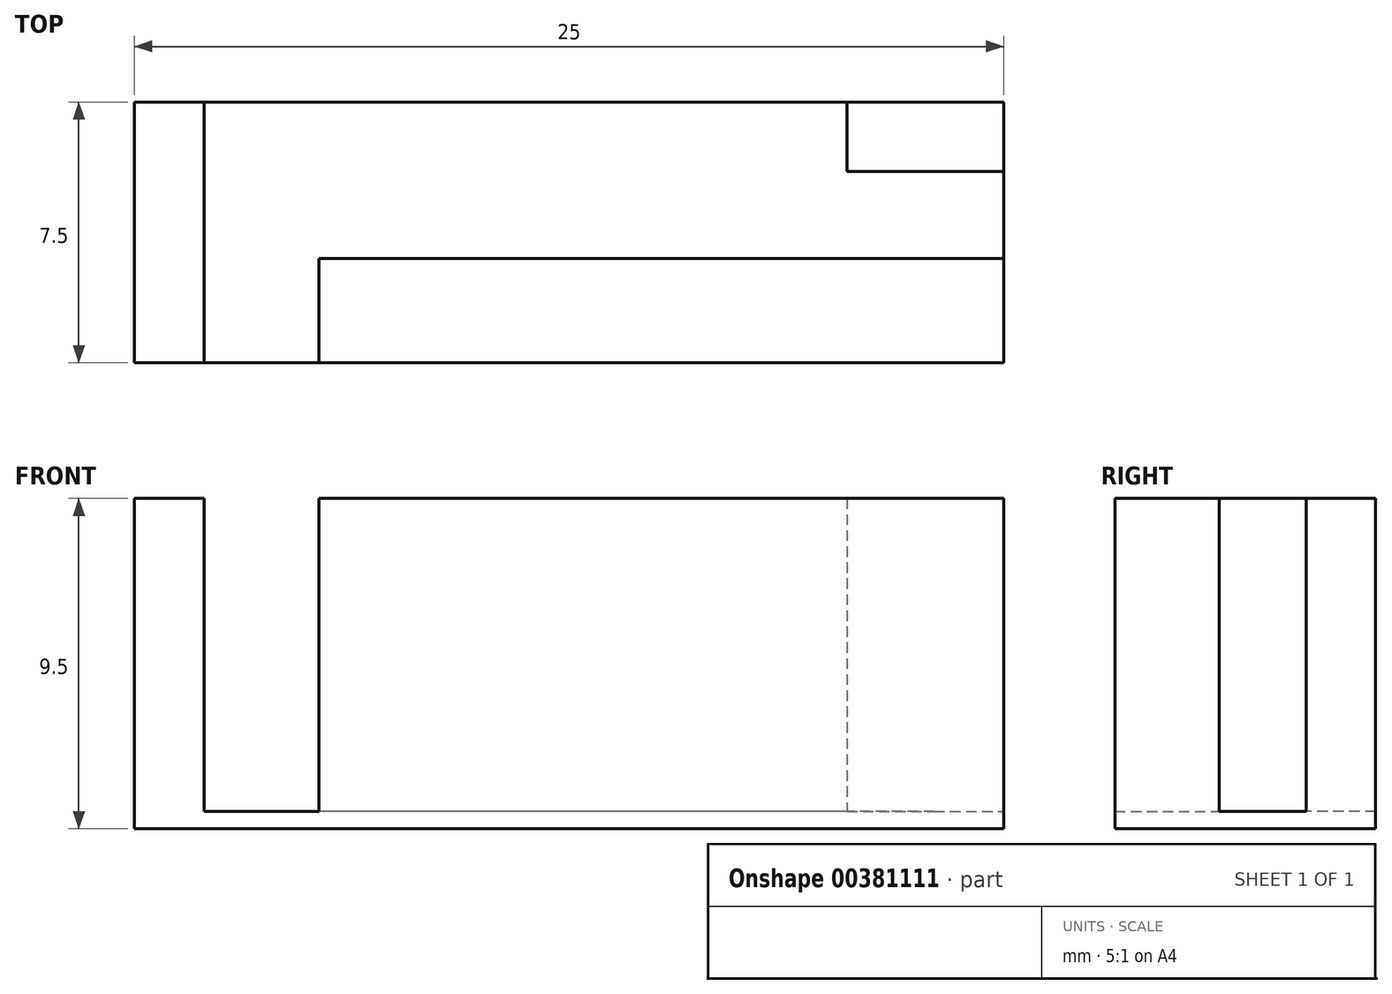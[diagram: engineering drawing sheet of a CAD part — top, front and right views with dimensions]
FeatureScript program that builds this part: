
annotation { "Feature Type Name" : "Feature", "Feature Type Description" : "" }
export const myFeature = defineFeature(function(context is Context, id is Id, definition is map)
    precondition{}
    {
        {
            var Q0;
            Q0=qCreatedBy(makeId("Top.planeOp"),FACE);
            var sketch = newSketch(context, id + "F0", { "sketchPlane" : qUnion([Q0])});
            skCircle(sketch, "E0", {"center": v(0, 0) * mm, "radius": 2.5 * mm});
            skCircle(sketch, "E1", {"center": v(53, 0) * mm, "radius": 2.5 * mm});
            skLineSegment(sketch, "E2.bottom", {"start": v(-4.5, 4.5) * mm, "end": v(57.5, 4.5) * mm});
            skLineSegment(sketch, "E2.top", {"start": v(-4.5, -5.5) * mm, "end": v(57.5, -5.5) * mm});
            skLineSegment(sketch, "E2.left", {"start": v(-4.5, 4.5) * mm, "end": v(-4.5, -5.5) * mm});
            skLineSegment(sketch, "E2.right", {"start": v(57.5, 4.5) * mm, "end": v(57.5, -5.5) * mm});
            skSolve(sketch);
        }
        {
            var Q0;
            Q0=qSketchRegion(id+"F0",true);
            extrude(context, id + "F1", {"entities" : qUnion([Q0]), "depth" : 2.5 * mm});
        }
        {
            var Q0;
            Q0=makeQuery(id+"F1.opExtrude","CAP_FACE",FACE,{"disambiguationData":[OSD([sQuery(id+"F0.wireOp",EDGE,"E0"),sQuery(id+"F0.wireOp",EDGE,"E1"),sQuery(id+"F0.wireOp",EDGE,"E2.bottom"),sQuery(id+"F0.wireOp",EDGE,"E2.top"),sQuery(id+"F0.wireOp",EDGE,"E2.left"),sQuery(id+"F0.wireOp",EDGE,"E2.right")])],"isStart":false});
            var sketch = newSketch(context, id + "F2", { "sketchPlane" : qUnion([Q0])});
            skLineSegment(sketch, "E3.bottom", {"start": v(36.03, -5.5) * mm, "end": v(16.98, -5.5) * mm});
            skLineSegment(sketch, "E3.top", {"start": v(36.03, -1.5) * mm, "end": v(16.98, -1.5) * mm});
            skLineSegment(sketch, "E3.left", {"start": v(36.03, -5.5) * mm, "end": v(36.03, -1.5) * mm});
            skLineSegment(sketch, "E3.right", {"start": v(16.98, -5.5) * mm, "end": v(16.98, -1.5) * mm});
            skSolve(sketch);
        }
        {
            var Q0;
            Q0=qSketchRegion(id+"F2",true);
            extrude(context, id + "F3", {"entities" : qUnion([Q0]), "operationType" : NewBodyOperationType.REMOVE, "oppositeDirection" : true, "depth" : 25.4 * mm});
        }
        {
            var Q0;
            Q0=makeQuery(id+"F3.boolean.opBoolean","COPY",EDGE,{"derivedFrom":makeQuery(id+"F3.opExtrude","SWEPT_EDGE",EDGE,{"disambiguationData":[OSD([sQuery(id+"F2.wireOp",EDGE,"E3.top"),sQuery(id+"F2.wireOp",EDGE,"E3.left")])]})});
            var Q1;
            Q1=makeQuery(id+"F3.boolean.opBoolean","COPY",EDGE,{"derivedFrom":makeQuery(id+"F3.opExtrude","SWEPT_EDGE",EDGE,{"disambiguationData":[OSD([sQuery(id+"F2.wireOp",EDGE,"E3.top"),sQuery(id+"F2.wireOp",EDGE,"E3.right")])]})});
            fillet(context, id + "F4", {"entities" : qUnion([Q0, Q1]), "radius" : 1.27 * mm, "tangentPropagation" : true, "allowEdgeOverflow" : false});
        }
        {
            var Q0;
            Q0=makeQuery(id+"F1.opExtrude","CAP_FACE",FACE,{"disambiguationData":[OSD([sQuery(id+"F0.wireOp",EDGE,"E0"),sQuery(id+"F0.wireOp",EDGE,"E1"),sQuery(id+"F0.wireOp",EDGE,"E2.bottom"),sQuery(id+"F0.wireOp",EDGE,"E2.top"),sQuery(id+"F0.wireOp",EDGE,"E2.left"),sQuery(id+"F0.wireOp",EDGE,"E2.right")])],"isStart":false});
            var sketch = newSketch(context, id + "F5", { "sketchPlane" : qUnion([Q0])});
            skLineSegment(sketch, "E4.bottom", {"start": v(39, 4.5) * mm, "end": v(14, 4.5) * mm});
            skLineSegment(sketch, "E4.top", {"start": v(39, 1.5) * mm, "end": v(14, 1.5) * mm});
            skLineSegment(sketch, "E4.left", {"start": v(39, 4.5) * mm, "end": v(39, 1.5) * mm});
            skLineSegment(sketch, "E4.right", {"start": v(14, 4.5) * mm, "end": v(14, 1.5) * mm});
            skSolve(sketch);
        }
        {
            var Q0;
            Q0=qSketchRegion(id+"F5",true);
            extrude(context, id + "F6", {"entities" : qUnion([Q0]), "operationType" : NewBodyOperationType.ADD, "depth" : 10 * mm});
        }
        {
            var Q0;
            Q0=makeQuery(id+"F6.boolean.opBoolean","MERGE",FACE,{"derivedFrom":[makeQuery(id+"F1.opExtrude","SWEPT_FACE",FACE,{"disambiguationData":[OSD([sQuery(id+"F0.wireOp",EDGE,"E2.bottom")])]}),makeQuery(id+"F6.opExtrude","SWEPT_FACE",FACE,{"disambiguationData":[OSD([sQuery(id+"F5.wireOp",EDGE,"E4.bottom")])]})]});
            var sketch = newSketch(context, id + "F7", { "sketchPlane" : qUnion([Q0])});
            skLineSegment(sketch, "E5.bottom", {"start": v(-37, 11.5) * mm, "end": v(-16, 11.5) * mm});
            skLineSegment(sketch, "E5.top", {"start": v(-37, 3.5) * mm, "end": v(-16, 3.5) * mm});
            skLineSegment(sketch, "E5.left", {"start": v(-37, 11.5) * mm, "end": v(-37, 3.5) * mm});
            skLineSegment(sketch, "E5.right", {"start": v(-16, 11.5) * mm, "end": v(-16, 3.5) * mm});
            skLineSegment(sketch, "E6.bottom", {"start": v(-39, 12.5) * mm, "end": v(-37, 12.5) * mm});
            skLineSegment(sketch, "E6.top", {"start": v(-39, 2.5) * mm, "end": v(-37, 2.5) * mm});
            skLineSegment(sketch, "E6.left", {"start": v(-39, 12.5) * mm, "end": v(-39, 2.5) * mm});
            skLineSegment(sketch, "E6.right", {"start": v(-37, 12.5) * mm, "end": v(-37, 2.5) * mm});
            skLineSegment(sketch, "E7.bottom", {"start": v(-14, 12.5) * mm, "end": v(-16, 12.5) * mm});
            skLineSegment(sketch, "E7.top", {"start": v(-14, 2.5) * mm, "end": v(-16, 2.5) * mm});
            skLineSegment(sketch, "E7.left", {"start": v(-14, 12.5) * mm, "end": v(-14, 2.5) * mm});
            skLineSegment(sketch, "E7.right", {"start": v(-16, 12.5) * mm, "end": v(-16, 2.5) * mm});
            skLineSegment(sketch, "E8.bottom", {"start": v(-37, 2.5) * mm, "end": v(-16, 2.5) * mm});
            skLineSegment(sketch, "E8.left", {"start": v(-37, 2.5) * mm, "end": v(-37, 3.5) * mm});
            skLineSegment(sketch, "E8.right", {"start": v(-16, 2.5) * mm, "end": v(-16, 3.5) * mm});
            skSolve(sketch);
        }
        {
            var Q0;
            {var subQ2=sQuery(id+"F7.wireOp",EDGE,"E6.bottom");Q0=makeQuery(id+"F7.imprint","IMPRINT",FACE,{"disambiguationData":[TD([[makeQuery(id+"F7.imprint","IMPRINT",EDGE,{"derivedFrom":subQ2}),1.0]])]});}
            var Q1;
            {var subQ2=sQuery(id+"F7.wireOp",EDGE,"E7.bottom");Q1=makeQuery(id+"F7.imprint","IMPRINT",FACE,{"disambiguationData":[TD([[makeQuery(id+"F7.imprint","IMPRINT",EDGE,{"derivedFrom":subQ2}),1.0]])]});}
            var Q2;
            Q2=makeQuery(id+"F7.imprint","IMPRINT",FACE,{"disambiguationData":[TD([[makeQuery(id+"F7.imprint","IMPRINT",EDGE,{"derivedFrom":sQuery(id+"F7.wireOp",EDGE,"E8.bottom")}),1.0]])]});
            extrude(context, id + "F8", {"entities" : qUnion([Q0, Q1, Q2]), "operationType" : NewBodyOperationType.ADD, "depth" : 4.5 * mm});
        }
        {
            var Q0;
            {var subQ1=sQuery(id+"F0.wireOp",EDGE,"E2.left");var subQ3=sQuery(id+"F0.wireOp",EDGE,"E2.bottom");Q0=makeQuery(id+"F8.boolean.opBoolean","SPLIT",FACE,{"disambiguationData":[TD([makeQuery(id+"F1.opExtrude","SWEPT_FACE",FACE,{"disambiguationData":[OSD([subQ1])]})])],"derivedFrom":makeQuery(id+"F6.boolean.opBoolean","MERGE",FACE,{"derivedFrom":[makeQuery(id+"F1.opExtrude","SWEPT_FACE",FACE,{"disambiguationData":[OSD([subQ3])]}),makeQuery(id+"F6.opExtrude","SWEPT_FACE",FACE,{"disambiguationData":[OSD([sQuery(id+"F5.wireOp",EDGE,"E4.bottom")])]})]})});}
            var sketch = newSketch(context, id + "F9", { "sketchPlane" : qUnion([Q0])});
            skSolve(sketch);
        }
        {
            var Q0;
            {var subQ2=sQuery(id+"F0.wireOp",EDGE,"E2.bottom");Q0=makeQuery(id+"F9.imprint","IMPRINT",FACE,{"disambiguationData":[TD([[makeQuery(id+"F9.imprint","IMPRINT",EDGE,{"derivedFrom":makeQuery(id+"F1.opExtrude","CAP_EDGE",EDGE,{"disambiguationData":[OSD([subQ2])],"isStart":true})}),-1.0]])]});}
            extrude(context, id + "F10", {"entities" : qUnion([Q0]), "operationType" : NewBodyOperationType.ADD, "depth" : 4.5 * mm});
        }
        {
            var Q0;
            {var subQ0=sQuery(id+"F5.wireOp",EDGE,"E4.bottom");Q0=makeQuery(id+"F8.boolean.opBoolean","SPLIT",FACE,{"disambiguationData":[TD([makeQuery(id+"F8.opExtrude","SWEPT_FACE",FACE,{"disambiguationData":[OSD([sQuery(id+"F7.wireOp",EDGE,"E6.bottom")])]})])],"derivedFrom":makeQuery(id+"F6.boolean.opBoolean","MERGE",FACE,{"derivedFrom":[makeQuery(id+"F1.opExtrude","SWEPT_FACE",FACE,{"disambiguationData":[OSD([sQuery(id+"F0.wireOp",EDGE,"E2.bottom")])]}),makeQuery(id+"F6.opExtrude","SWEPT_FACE",FACE,{"disambiguationData":[OSD([subQ0])]})]})});}
            var sketch = newSketch(context, id + "F11", { "sketchPlane" : qUnion([Q0])});
            skLineSegment(sketch, "E9.bottom", {"start": v(-16, 3.5) * mm, "end": v(-19.3, 3.5) * mm});
            skLineSegment(sketch, "E9.top", {"start": v(-16, 12.5) * mm, "end": v(-19.3, 12.5) * mm});
            skLineSegment(sketch, "E9.left", {"start": v(-16, 3.5) * mm, "end": v(-16, 12.5) * mm});
            skLineSegment(sketch, "E9.right", {"start": v(-19.3, 3.5) * mm, "end": v(-19.3, 12.5) * mm});
            skSolve(sketch);
        }
        {
            var Q0;
            Q0=qSketchRegion(id+"F11",true);
            extrude(context, id + "F12", {"entities" : qUnion([Q0]), "operationType" : NewBodyOperationType.REMOVE, "oppositeDirection" : true, "depth" : 25.4 * mm});
        }
        {
            var Q0;
            Q0=makeQuery(id+"F8.opExtrude","SWEPT_FACE",FACE,{"disambiguationData":[OSD([sQuery(id+"F7.wireOp",EDGE,"E6.right")])]});
            var sketch = newSketch(context, id + "F13", { "sketchPlane" : qUnion([Q0])});
            skLineSegment(sketch, "E10.bottom", {"start": v(-9, 12.5) * mm, "end": v(-7, 12.5) * mm});
            skLineSegment(sketch, "E10.top", {"start": v(-9, 3.5) * mm, "end": v(-7, 3.5) * mm});
            skLineSegment(sketch, "E10.left", {"start": v(-9, 12.5) * mm, "end": v(-9, 3.5) * mm});
            skLineSegment(sketch, "E10.right", {"start": v(-7, 12.5) * mm, "end": v(-7, 3.5) * mm});
            skSolve(sketch);
        }
        {
            var Q0;
            Q0=qSketchRegion(id+"F13",true);
            extrude(context, id + "F14", {"entities" : qUnion([Q0]), "operationType" : NewBodyOperationType.ADD, "depth" : 2.5 * mm});
        }
        {
            var Q0;
            {var subQ0=sQuery(id+"F5.wireOp",EDGE,"E4.left");var subQ1=sQuery(id+"F5.wireOp",EDGE,"E4.top");var subQ2=sQuery(id+"F5.wireOp",EDGE,"E4.bottom");var subQ3=sQuery(id+"F0.wireOp",EDGE,"E2.bottom");var subQ6=sQuery(id+"F7.wireOp",EDGE,"E7.bottom");var subQ10=sQuery(id+"F7.wireOp",EDGE,"E6.bottom");Q0=makeQuery(id+"F14.boolean.opBoolean","MERGE",FACE,{"derivedFrom":[makeQuery(id+"F12.boolean.opBoolean","SPLIT",FACE,{"disambiguationData":[TD([makeQuery(id+"F1.opExtrude","SWEPT_FACE",FACE,{"disambiguationData":[OSD([subQ3])]})])],"derivedFrom":makeQuery(id+"F8.boolean.opBoolean","MERGE",FACE,{"derivedFrom":[makeQuery(id+"F6.opExtrude","CAP_FACE",FACE,{"disambiguationData":[OSD([subQ2,subQ1,subQ0,sQuery(id+"F5.wireOp",EDGE,"E4.right")])],"isStart":false}),makeQuery(id+"F8.opExtrude","SWEPT_FACE",FACE,{"disambiguationData":[OSD([subQ10])]}),makeQuery(id+"F8.opExtrude","SWEPT_FACE",FACE,{"disambiguationData":[OSD([subQ6])]})]})}),makeQuery(id+"F14.opExtrude","SWEPT_FACE",FACE,{"disambiguationData":[OSD([sQuery(id+"F13.wireOp",EDGE,"E10.bottom")])]})]});}
            var sketch = newSketch(context, id + "F15", { "sketchPlane" : qUnion([Q0])});
            skLineSegment(sketch, "E11.bottom", {"start": v(39, 1.5) * mm, "end": v(14, 1.5) * mm});
            skLineSegment(sketch, "E11.top", {"start": v(39, 9) * mm, "end": v(14, 9) * mm});
            skLineSegment(sketch, "E11.left", {"start": v(39, 1.5) * mm, "end": v(39, 9) * mm});
            skLineSegment(sketch, "E11.right", {"start": v(14, 1.5) * mm, "end": v(14, 9) * mm});
            skLineSegment(sketch, "E12.bottom", {"start": v(-4.5, 9) * mm, "end": v(57.5, 9) * mm});
            skLineSegment(sketch, "E12.top", {"start": v(-4.5, -5.5) * mm, "end": v(57.5, -5.5) * mm});
            skLineSegment(sketch, "E12.left", {"start": v(-4.5, 9) * mm, "end": v(-4.5, -5.5) * mm});
            skLineSegment(sketch, "E12.right", {"start": v(57.5, 9) * mm, "end": v(57.5, -5.5) * mm});
            skSolve(sketch);
        }
        {
            var Q0;
            {var subQ1=sQuery(id+"F15.wireOp",EDGE,"E11.left");Q0=makeQuery(id+"F15.imprint","IMPRINT",FACE,{"disambiguationData":[TD([[makeQuery(id+"F15.imprint","IMPRINT",EDGE,{"derivedFrom":subQ1}),1.0]])]});}
            extrude(context, id + "F16", {"entities" : qUnion([Q0]), "operationType" : NewBodyOperationType.REMOVE, "oppositeDirection" : true, "depth" : 25.4 * mm});
        }
        {
            var Q0;
            {var subQ0=sQuery(id+"F0.wireOp",EDGE,"E2.bottom");Q0=makeQuery(id+"F10.boolean.opBoolean","MERGE",FACE,{"derivedFrom":[makeQuery(id+"F1.opExtrude","CAP_FACE",FACE,{"disambiguationData":[OSD([sQuery(id+"F0.wireOp",EDGE,"E0"),sQuery(id+"F0.wireOp",EDGE,"E1"),subQ0,sQuery(id+"F0.wireOp",EDGE,"E2.top"),sQuery(id+"F0.wireOp",EDGE,"E2.left"),sQuery(id+"F0.wireOp",EDGE,"E2.right")])],"isStart":true}),makeQuery(id+"F10.opExtrude","SWEPT_FACE",FACE,{"disambiguationData":[OSD([subQ0])]})]});}
            extrude(context, id + "F17", {"entities" : qUnion([Q0]), "operationType" : NewBodyOperationType.REMOVE, "oppositeDirection" : true, "depth" : 3 * mm});
        }
        {
            var Q0;
            {var subQ0=sQuery(id+"F5.wireOp",EDGE,"E4.left");var subQ1=sQuery(id+"F5.wireOp",EDGE,"E4.top");var subQ2=sQuery(id+"F5.wireOp",EDGE,"E4.bottom");var subQ3=sQuery(id+"F0.wireOp",EDGE,"E2.bottom");var subQ6=sQuery(id+"F7.wireOp",EDGE,"E7.bottom");var subQ10=sQuery(id+"F7.wireOp",EDGE,"E6.bottom");Q0=makeQuery(id+"F14.boolean.opBoolean","MERGE",FACE,{"derivedFrom":[makeQuery(id+"F12.boolean.opBoolean","SPLIT",FACE,{"disambiguationData":[TD([makeQuery(id+"F1.opExtrude","SWEPT_FACE",FACE,{"disambiguationData":[OSD([subQ3])]})])],"derivedFrom":makeQuery(id+"F8.boolean.opBoolean","MERGE",FACE,{"derivedFrom":[makeQuery(id+"F6.opExtrude","CAP_FACE",FACE,{"disambiguationData":[OSD([subQ2,subQ1,subQ0,sQuery(id+"F5.wireOp",EDGE,"E4.right")])],"isStart":false}),makeQuery(id+"F8.opExtrude","SWEPT_FACE",FACE,{"disambiguationData":[OSD([subQ10])]}),makeQuery(id+"F8.opExtrude","SWEPT_FACE",FACE,{"disambiguationData":[OSD([subQ6])]})]})}),makeQuery(id+"F14.opExtrude","SWEPT_FACE",FACE,{"disambiguationData":[OSD([sQuery(id+"F13.wireOp",EDGE,"E10.bottom")])]})]});}
            var sketch = newSketch(context, id + "F18", { "sketchPlane" : qUnion([Q0])});
            skLineSegment(sketch, "E13.bottom", {"start": v(37, 7) * mm, "end": v(39, 7) * mm});
            skLineSegment(sketch, "E13.top", {"start": v(37, 4.5) * mm, "end": v(39, 4.5) * mm});
            skLineSegment(sketch, "E13.left", {"start": v(37, 7) * mm, "end": v(37, 4.5) * mm});
            skLineSegment(sketch, "E13.right", {"start": v(39, 7) * mm, "end": v(39, 4.5) * mm});
            skSolve(sketch);
        }
        {
            var Q0;
            Q0 = qSketchRegion(id + "F18", true);
            extrude(context, id + "F19", {"entities" : qUnion([Q0]), "operationType" : NewBodyOperationType.REMOVE, "oppositeDirection" : true, "depth" : 9 * mm});
        }
    });
